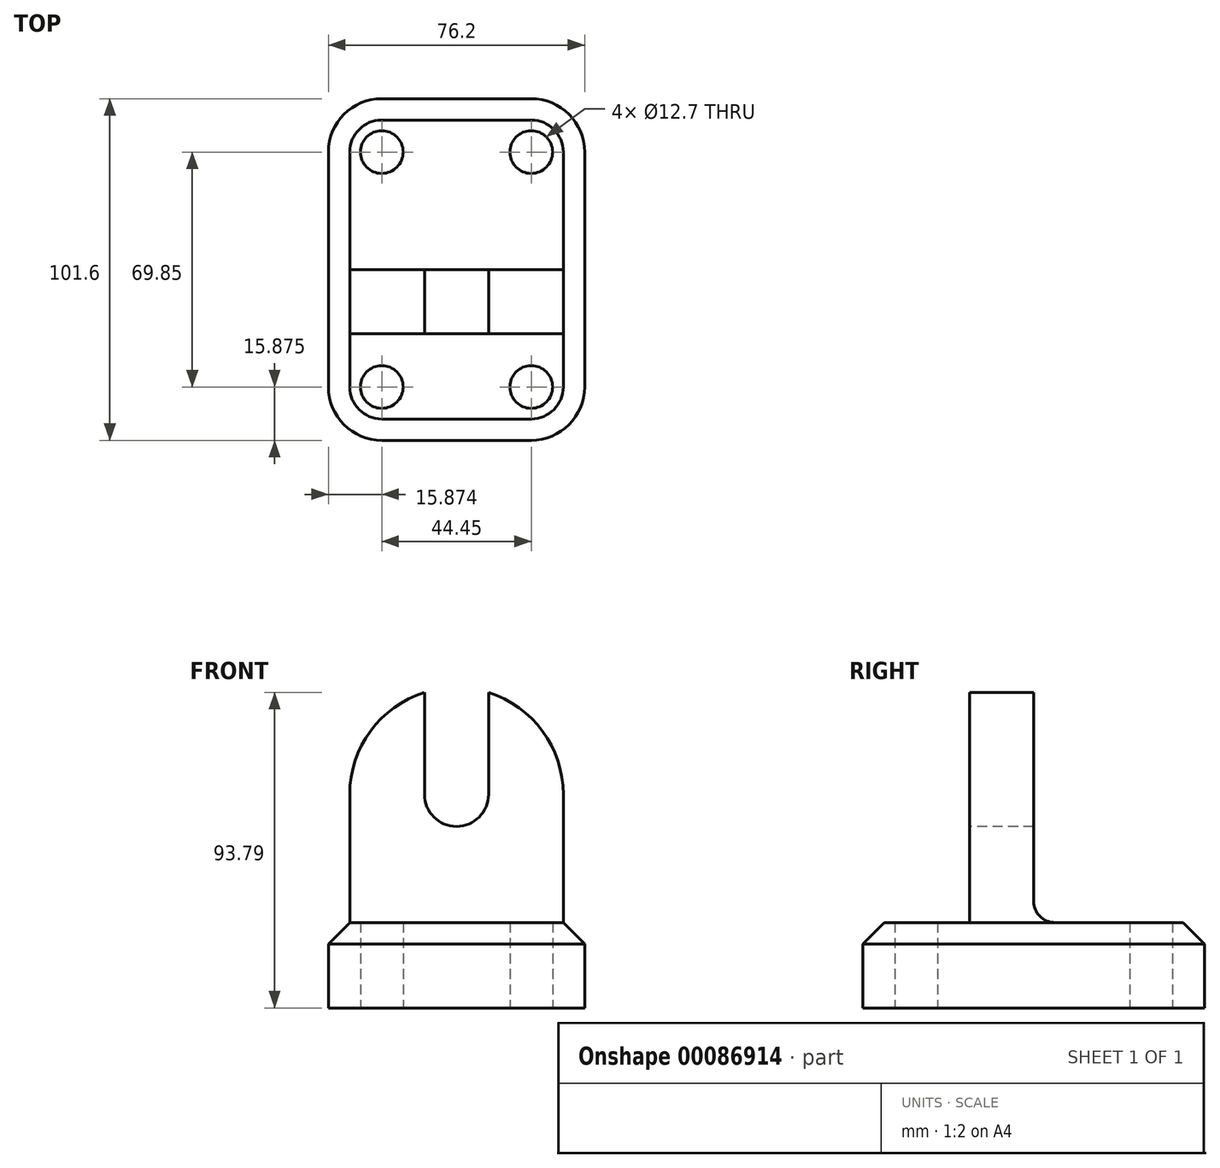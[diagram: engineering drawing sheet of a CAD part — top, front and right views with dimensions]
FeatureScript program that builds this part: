
annotation { "Feature Type Name" : "Feature", "Feature Type Description" : "" }
export const myFeature = defineFeature(function(context is Context, id is Id, definition is map)
    precondition{}
    {
        {
            var Q0;
            Q0=qCreatedBy(makeId("Top.planeOp"),FACE);
            var sketch = newSketch(context, id + "F0", { "sketchPlane" : qUnion([Q0])});
            skLineSegment(sketch, "E0.bottom", {"start": v(-23.1, 42) * mm, "end": v(21.34, 42) * mm});
            skLineSegment(sketch, "E0.top", {"start": v(-23.1, -59.6) * mm, "end": v(21.34, -59.6) * mm});
            skLineSegment(sketch, "E0.left", {"start": v(-38.98, 26.13) * mm, "end": v(-38.98, -43.72) * mm});
            skLineSegment(sketch, "E0.right", {"start": v(37.22, 26.13) * mm, "end": v(37.22, -43.72) * mm});
            skPoint(sketch, "E1.visualSharp", {"position": v(-38.98, 42) * mm});
            skArc(sketch, "E1.filletArc", {"start": v(-23.1, 42) * mm, "mid": v(-34.33, 37.35) * mm, "end": v(-38.98, 26.13) * mm});
            skPoint(sketch, "E2.visualSharp", {"position": v(37.22, 42) * mm});
            skArc(sketch, "E2.filletArc", {"start": v(37.22, 26.13) * mm, "mid": v(32.57, 37.35) * mm, "end": v(21.34, 42) * mm});
            skPoint(sketch, "E3.visualSharp", {"position": v(37.22, -59.6) * mm});
            skArc(sketch, "E3.filletArc", {"start": v(21.34, -59.6) * mm, "mid": v(32.57, -54.95) * mm, "end": v(37.22, -43.72) * mm});
            skPoint(sketch, "E4.visualSharp", {"position": v(-38.98, -59.6) * mm});
            skArc(sketch, "E4.filletArc", {"start": v(-38.98, -43.72) * mm, "mid": v(-34.33, -54.95) * mm, "end": v(-23.1, -59.6) * mm});
            skSolve(sketch);
        }
        {
            var Q0;
            Q0=makeQuery(id+"F0.imprint","IMPRINT",FACE,{"disambiguationData":[TD([[makeQuery(id+"F0.imprint","IMPRINT",EDGE,{"derivedFrom":sQuery(id+"F0.wireOp",EDGE,"E0.bottom")}),-1.0]])]});
            extrude(context, id + "F1", {"entities" : qUnion([Q0]), "depth" : 25.4 * mm});
        }
        {
            var Q0;
            Q0=makeQuery(id+"F1.opExtrude","CAP_EDGE",EDGE,{"disambiguationData":[OSD([sQuery(id+"F0.wireOp",EDGE,"E0.bottom")])],"isStart":false});
            chamfer(context, id + "F2", {"entities" : qUnion([Q0]), "width" : 6.35 * mm, "tangentPropagation" : true});
        }
        {
            var Q0;
            Q0=makeQuery(id+"F1.opExtrude","CAP_FACE",FACE,{"disambiguationData":[OSD([sQuery(id+"F0.wireOp",EDGE,"E0.bottom"),sQuery(id+"F0.wireOp",EDGE,"E0.top"),sQuery(id+"F0.wireOp",EDGE,"E0.left"),sQuery(id+"F0.wireOp",EDGE,"E0.right"),sQuery(id+"F0.wireOp",EDGE,"E1.filletArc"),sQuery(id+"F0.wireOp",EDGE,"E2.filletArc"),sQuery(id+"F0.wireOp",EDGE,"E3.filletArc"),sQuery(id+"F0.wireOp",EDGE,"E4.filletArc")])],"isStart":false});
            var sketch = newSketch(context, id + "F3", { "sketchPlane" : qUnion([Q0])});
            skLineSegment(sketch, "E5.bottom", {"start": v(-32.63, -8.8) * mm, "end": v(30.87, -8.8) * mm});
            skLineSegment(sketch, "E5.top", {"start": v(-32.63, -27.85) * mm, "end": v(30.87, -27.85) * mm});
            skLineSegment(sketch, "E5.left", {"start": v(-32.63, -8.8) * mm, "end": v(-32.63, -27.85) * mm});
            skLineSegment(sketch, "E5.right", {"start": v(30.87, -8.8) * mm, "end": v(30.87, -27.85) * mm});
            skSolve(sketch);
        }
        {
            var Q0;
            Q0=qSketchRegion(id+"F3",true);
            extrude(context, id + "F4", {"entities" : qUnion([Q0]), "operationType" : NewBodyOperationType.ADD, "depth" : 95.25 * mm});
        }
        {
            var Q0;
            Q0=makeQuery(id+"F4.opExtrude","SWEPT_FACE",FACE,{"disambiguationData":[OSD([sQuery(id+"F3.wireOp",EDGE,"E5.top")])]});
            var sketch = newSketch(context, id + "F5", { "sketchPlane" : qUnion([Q0])});
            skPoint(sketch, "E6", {"position": v(-0.88, 63.5) * mm});
            skArc(sketch, "E7", {"start": v(30.87, 63.5) * mm, "mid": v(-0.88, 95.25) * mm, "end": v(-32.63, 63.5) * mm});
            skCircle(sketch, "E8", {"center": v(-0.88, 63.5) * mm, "radius": 9.53 * mm});
            skLineSegment(sketch, "E9", {"start": v(8.64, 25.4) * mm, "end": v(8.64, 93.79) * mm});
            skLineSegment(sketch, "E10", {"start": v(-10.4, 93.79) * mm, "end": v(-10.4, 25.4) * mm});
            skSolve(sketch);
        }
        {
            var Q0;
            {var subQ0=sQuery(id+"F5.wireOp",EDGE,"E7");var subQ1=sQuery(id+"F3.wireOp",EDGE,"E5.top");var subQ4=makeQuery(id+"F4.opExtrude","CAP_EDGE",EDGE,{"disambiguationData":[OSD([subQ1])],"isStart":false});var subQ5=makeQuery(id+"F5.imprint","INTERSECT",VERTEX,{"derivedFrom":[subQ4,subQ0]});Q0=makeQuery(id+"F5.imprint","IMPRINT",FACE,{"disambiguationData":[TD([[makeQuery(id+"F5.imprint","IMPRINT",EDGE,{"disambiguationData":[TD([[subQ5,-1.0]])],"derivedFrom":subQ0}),-1.0]])]});}
            var Q1;
            {var subQ0=sQuery(id+"F5.wireOp",EDGE,"E7");var subQ1=sQuery(id+"F3.wireOp",EDGE,"E5.top");var subQ4=makeQuery(id+"F4.opExtrude","CAP_EDGE",EDGE,{"disambiguationData":[OSD([subQ1])],"isStart":false});var subQ5=makeQuery(id+"F5.imprint","INTERSECT",VERTEX,{"derivedFrom":[subQ4,subQ0]});Q1=makeQuery(id+"F5.imprint","IMPRINT",FACE,{"disambiguationData":[TD([[makeQuery(id+"F5.imprint","IMPRINT",EDGE,{"disambiguationData":[TD([[subQ5,1.0]])],"derivedFrom":subQ0}),-1.0]])]});}
            extrude(context, id + "F6", {"entities" : qUnion([Q0, Q1]), "operationType" : NewBodyOperationType.REMOVE, "oppositeDirection" : true, "depth" : 25.4 * mm});
        }
        {
            var Q0;
            {var subQ0=sQuery(id+"F5.wireOp",EDGE,"E8");var subQ1=makeQuery(id+"F5.imprint","INTERSECT",VERTEX,{"derivedFrom":[subQ0,sQuery(id+"F5.wireOp",EDGE,"E9")]});Q0=makeQuery(id+"F5.imprint","IMPRINT",FACE,{"disambiguationData":[TD([[makeQuery(id+"F5.imprint","IMPRINT",EDGE,{"disambiguationData":[TD([[subQ1,-1.0]])],"derivedFrom":subQ0}),1.0]])]});}
            var Q1;
            {var subQ0=sQuery(id+"F5.wireOp",EDGE,"E9");var subQ1=sQuery(id+"F5.wireOp",EDGE,"E7");var subQ2=makeQuery(id+"F5.imprint","INTERSECT",VERTEX,{"derivedFrom":[subQ1,subQ0]});Q1=makeQuery(id+"F5.imprint","IMPRINT",FACE,{"disambiguationData":[TD([[makeQuery(id+"F5.imprint","IMPRINT",EDGE,{"disambiguationData":[TD([[subQ2,-1.0]])],"derivedFrom":subQ1}),1.0]])]});}
            extrude(context, id + "F7", {"entities" : qUnion([Q0, Q1]), "operationType" : NewBodyOperationType.REMOVE, "oppositeDirection" : true, "depth" : 25.4 * mm});
        }
        {
            var Q0;
            Q0=sQuery(id+"F0.wireOp",VERTEX,"E4.filletArc.center");
            var Q1;
            Q1=sQuery(id+"F0.wireOp",VERTEX,"E3.filletArc.center");
            var Q2;
            Q2=sQuery(id+"F0.wireOp",VERTEX,"E1.filletArc.center");
            var Q3;
            Q3=sQuery(id+"F0.wireOp",VERTEX,"E2.filletArc.center");
            var Q4;
            Q4=makeQuery(id+"F1.opExtrude","SWEPT_BODY",BODY,{"disambiguationData":[OSD([sQuery(id+"F0.wireOp",EDGE,"E0.bottom"),sQuery(id+"F0.wireOp",EDGE,"E0.top"),sQuery(id+"F0.wireOp",EDGE,"E0.left"),sQuery(id+"F0.wireOp",EDGE,"E0.right"),sQuery(id+"F0.wireOp",EDGE,"E1.filletArc"),sQuery(id+"F0.wireOp",EDGE,"E2.filletArc"),sQuery(id+"F0.wireOp",EDGE,"E3.filletArc"),sQuery(id+"F0.wireOp",EDGE,"E4.filletArc")])]});
            hole(context, id + "F8", {"style" : HoleStyle.SIMPLE, "endStyle" : HoleEndStyle.THROUGH, "oppositeDirection" : true, "holeDiameter" : 12.7 * mm, "locations" : qUnion([Q0, Q1, Q2, Q3]), "scope" : qUnion([Q4]), "isTappedThrough" : true});
        }
        {
            var Q0;
            Q0=makeQuery(id+"F4.opExtrude","CAP_EDGE",EDGE,{"disambiguationData":[OSD([sQuery(id+"F3.wireOp",EDGE,"E5.bottom")])],"isStart":true});
            var Q1;
            Q1=makeQuery(id+"F4.opExtrude","CAP_EDGE",EDGE,{"disambiguationData":[OSD([sQuery(id+"F3.wireOp",EDGE,"E5.top")])],"isStart":true});
            fillet(context, id + "F9", {"entities" : qUnion([Q0, Q1]), "radius" : 6.35 * mm, "tangentPropagation" : true, "allowEdgeOverflow" : false});
        }
    });
